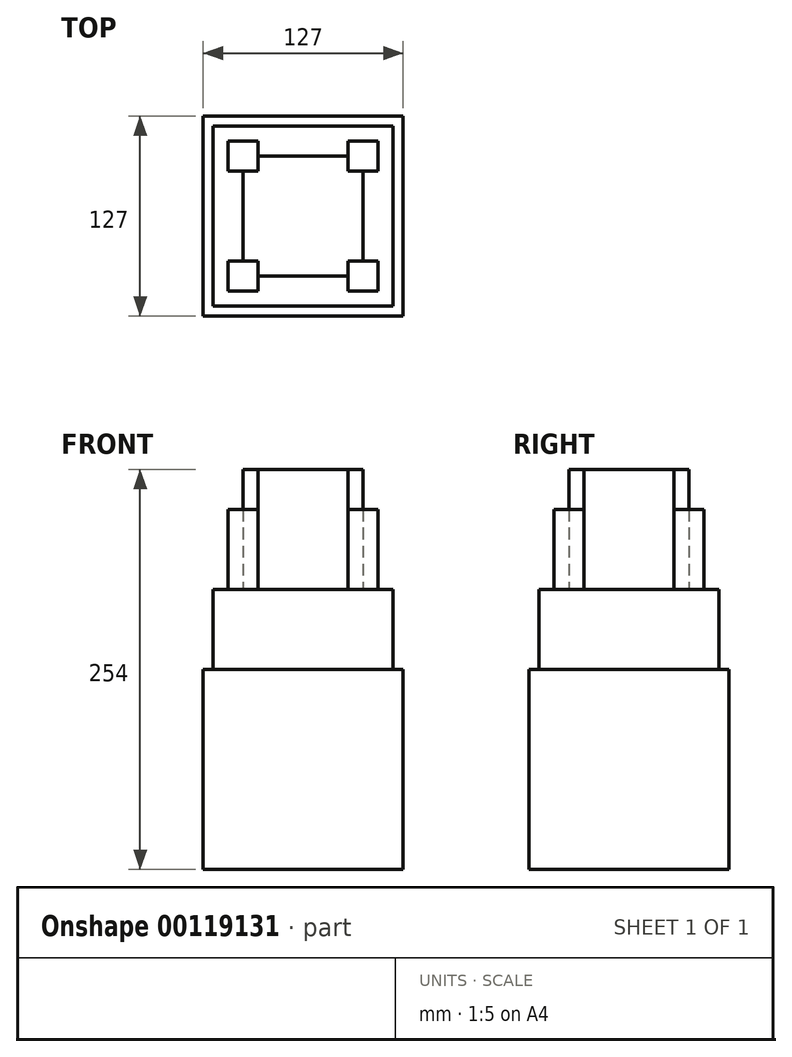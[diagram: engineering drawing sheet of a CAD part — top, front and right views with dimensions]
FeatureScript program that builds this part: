
annotation { "Feature Type Name" : "Feature", "Feature Type Description" : "" }
export const myFeature = defineFeature(function(context is Context, id is Id, definition is map)
    precondition{}
    {
        {
            var Q0;
            Q0=qCreatedBy(makeId("Top.planeOp"),FACE);
            var sketch = newSketch(context, id + "F0", { "sketchPlane" : qUnion([Q0])});
            skLineSegment(sketch, "E0.bottom", {"start": v(-63.5, 63.5) * mm, "end": v(63.5, 63.5) * mm});
            skLineSegment(sketch, "E0.top", {"start": v(-63.5, -63.5) * mm, "end": v(63.5, -63.5) * mm});
            skLineSegment(sketch, "E0.left", {"start": v(-63.5, 63.5) * mm, "end": v(-63.5, -63.5) * mm});
            skLineSegment(sketch, "E0.right", {"start": v(63.5, 63.5) * mm, "end": v(63.5, -63.5) * mm});
            skPoint(sketch, "E0.middle", {"position": v(0, 0) * mm});
            skLineSegment(sketch, "E1.bottom", {"start": v(-57.15, 57.15) * mm, "end": v(57.15, 57.15) * mm});
            skLineSegment(sketch, "E1.top", {"start": v(-57.15, -57.15) * mm, "end": v(57.15, -57.15) * mm});
            skLineSegment(sketch, "E1.left", {"start": v(-57.15, 57.15) * mm, "end": v(-57.15, -57.15) * mm});
            skLineSegment(sketch, "E1.right", {"start": v(57.15, 57.15) * mm, "end": v(57.15, -57.15) * mm});
            skLineSegment(sketch, "E2.bottom", {"start": v(-38.1, 38.1) * mm, "end": v(38.1, 38.1) * mm});
            skLineSegment(sketch, "E2.top", {"start": v(-38.1, -38.1) * mm, "end": v(38.1, -38.1) * mm});
            skLineSegment(sketch, "E2.left", {"start": v(-38.1, 38.1) * mm, "end": v(-38.1, -38.1) * mm});
            skLineSegment(sketch, "E2.right", {"start": v(38.1, 38.1) * mm, "end": v(38.1, -38.1) * mm});
            skLineSegment(sketch, "E3.bottom", {"start": v(-47.62, 47.62) * mm, "end": v(-28.57, 47.62) * mm});
            skLineSegment(sketch, "E3.top", {"start": v(-47.62, 28.57) * mm, "end": v(-28.57, 28.57) * mm});
            skLineSegment(sketch, "E3.left", {"start": v(-47.62, 47.62) * mm, "end": v(-47.62, 28.57) * mm});
            skLineSegment(sketch, "E3.right", {"start": v(-28.57, 47.62) * mm, "end": v(-28.57, 28.57) * mm});
            skPoint(sketch, "E3.middle", {"position": v(-38.1, 38.1) * mm});
            skLineSegment(sketch, "E4.bottom", {"start": v(-47.63, -47.62) * mm, "end": v(-28.58, -47.62) * mm});
            skLineSegment(sketch, "E4.top", {"start": v(-47.63, -28.57) * mm, "end": v(-28.58, -28.57) * mm});
            skLineSegment(sketch, "E4.left", {"start": v(-47.63, -47.62) * mm, "end": v(-47.63, -28.57) * mm});
            skLineSegment(sketch, "E4.right", {"start": v(-28.58, -47.62) * mm, "end": v(-28.58, -28.57) * mm});
            skPoint(sketch, "E4.middle", {"position": v(-38.1, -38.1) * mm});
            skLineSegment(sketch, "E5.bottom", {"start": v(47.62, -47.62) * mm, "end": v(28.57, -47.62) * mm});
            skLineSegment(sketch, "E5.top", {"start": v(47.63, -28.58) * mm, "end": v(28.57, -28.58) * mm});
            skLineSegment(sketch, "E5.left", {"start": v(47.63, -47.63) * mm, "end": v(47.63, -28.57) * mm});
            skLineSegment(sketch, "E5.right", {"start": v(28.57, -47.63) * mm, "end": v(28.57, -28.58) * mm});
            skPoint(sketch, "E5.middle", {"position": v(38.1, -38.1) * mm});
            skLineSegment(sketch, "E6.bottom", {"start": v(28.58, 28.57) * mm, "end": v(47.63, 28.57) * mm});
            skLineSegment(sketch, "E6.top", {"start": v(28.58, 47.62) * mm, "end": v(47.63, 47.62) * mm});
            skLineSegment(sketch, "E6.left", {"start": v(28.58, 28.57) * mm, "end": v(28.58, 47.62) * mm});
            skLineSegment(sketch, "E6.right", {"start": v(47.63, 28.57) * mm, "end": v(47.63, 47.62) * mm});
            skPoint(sketch, "E6.middle", {"position": v(38.1, 38.1) * mm});
            skSolve(sketch);
        }
        {
            var Q0;
            {var subQ15=sQuery(id+"F0.wireOp",EDGE,"E3.right");var subQ19=sQuery(id+"F0.wireOp",EDGE,"E2.bottom");var subQ20=makeQuery(id+"F0.imprint","INTERSECT",VERTEX,{"derivedFrom":[subQ19,subQ15]});Q0=makeQuery(id+"F0.imprint","IMPRINT",FACE,{"disambiguationData":[TD([[makeQuery(id+"F0.imprint","IMPRINT",EDGE,{"disambiguationData":[TD([[subQ20,-1.0]])],"derivedFrom":subQ19}),-1.0]])]});}
            extrude(context, id + "F1", {"entities" : qUnion([Q0]), "depth" : 254 * mm});
        }
        {
            var Q0;
            {var subQ8=sQuery(id+"F0.wireOp",EDGE,"E3.bottom");Q0=makeQuery(id+"F0.imprint","IMPRINT",FACE,{"disambiguationData":[TD([[makeQuery(id+"F0.imprint","IMPRINT",EDGE,{"derivedFrom":subQ8}),-1.0]])]});}
            var Q1;
            {var subQ0=sQuery(id+"F0.wireOp",EDGE,"E2.left");var subQ1=sQuery(id+"F0.wireOp",EDGE,"E2.bottom");var subQ2=makeQuery(id+"F0.imprint","INTERSECT",VERTEX,{"derivedFrom":[subQ1,subQ0]});Q1=makeQuery(id+"F0.imprint","IMPRINT",FACE,{"disambiguationData":[TD([[makeQuery(id+"F0.imprint","IMPRINT",EDGE,{"disambiguationData":[TD([[subQ2,-1.0]])],"derivedFrom":subQ1}),-1.0]])]});}
            var Q2;
            {var subQ6=sQuery(id+"F0.wireOp",EDGE,"E4.bottom");Q2=makeQuery(id+"F0.imprint","IMPRINT",FACE,{"disambiguationData":[TD([[makeQuery(id+"F0.imprint","IMPRINT",EDGE,{"derivedFrom":subQ6}),1.0]])]});}
            var Q3;
            {var subQ0=sQuery(id+"F0.wireOp",EDGE,"E2.left");var subQ1=sQuery(id+"F0.wireOp",EDGE,"E2.top");var subQ2=makeQuery(id+"F0.imprint","INTERSECT",VERTEX,{"derivedFrom":[subQ1,subQ0]});Q3=makeQuery(id+"F0.imprint","IMPRINT",FACE,{"disambiguationData":[TD([[makeQuery(id+"F0.imprint","IMPRINT",EDGE,{"disambiguationData":[TD([[subQ2,-1.0]])],"derivedFrom":subQ1}),1.0]])]});}
            var Q4;
            {var subQ4=sQuery(id+"F0.wireOp",EDGE,"E5.bottom");Q4=makeQuery(id+"F0.imprint","IMPRINT",FACE,{"disambiguationData":[TD([[makeQuery(id+"F0.imprint","IMPRINT",EDGE,{"derivedFrom":subQ4}),-1.0]])]});}
            var Q5;
            {var subQ0=sQuery(id+"F0.wireOp",EDGE,"E2.right");var subQ1=sQuery(id+"F0.wireOp",EDGE,"E2.top");var subQ2=makeQuery(id+"F0.imprint","INTERSECT",VERTEX,{"derivedFrom":[subQ1,subQ0]});Q5=makeQuery(id+"F0.imprint","IMPRINT",FACE,{"disambiguationData":[TD([[makeQuery(id+"F0.imprint","IMPRINT",EDGE,{"disambiguationData":[TD([[subQ2,1.0]])],"derivedFrom":subQ1}),1.0]])]});}
            var Q6;
            {var subQ6=sQuery(id+"F0.wireOp",EDGE,"E6.top");Q6=makeQuery(id+"F0.imprint","IMPRINT",FACE,{"disambiguationData":[TD([[makeQuery(id+"F0.imprint","IMPRINT",EDGE,{"derivedFrom":subQ6}),-1.0]])]});}
            var Q7;
            {var subQ0=sQuery(id+"F0.wireOp",EDGE,"E2.right");var subQ1=sQuery(id+"F0.wireOp",EDGE,"E2.bottom");var subQ2=makeQuery(id+"F0.imprint","INTERSECT",VERTEX,{"derivedFrom":[subQ1,subQ0]});Q7=makeQuery(id+"F0.imprint","IMPRINT",FACE,{"disambiguationData":[TD([[makeQuery(id+"F0.imprint","IMPRINT",EDGE,{"disambiguationData":[TD([[subQ2,1.0]])],"derivedFrom":subQ1}),-1.0]])]});}
            extrude(context, id + "F2", {"entities" : qUnion([Q0, Q1, Q2, Q3, Q4, Q5, Q6, Q7]), "operationType" : NewBodyOperationType.ADD, "depth" : 228.6 * mm});
        }
        {
            var Q0;
            Q0=makeQuery(id+"F0.imprint","IMPRINT",FACE,{"disambiguationData":[TD([[makeQuery(id+"F0.imprint","IMPRINT",EDGE,{"derivedFrom":sQuery(id+"F0.wireOp",EDGE,"E1.bottom")}),-1.0]])]});
            extrude(context, id + "F3", {"entities" : qUnion([Q0]), "operationType" : NewBodyOperationType.ADD, "depth" : 177.8 * mm});
        }
        {
            var Q0;
            Q0=makeQuery(id+"F0.imprint","IMPRINT",FACE,{"disambiguationData":[TD([[makeQuery(id+"F0.imprint","IMPRINT",EDGE,{"derivedFrom":sQuery(id+"F0.wireOp",EDGE,"E0.bottom")}),-1.0]])]});
            extrude(context, id + "F4", {"entities" : qUnion([Q0]), "operationType" : NewBodyOperationType.ADD, "depth" : 127 * mm});
        }
    });
